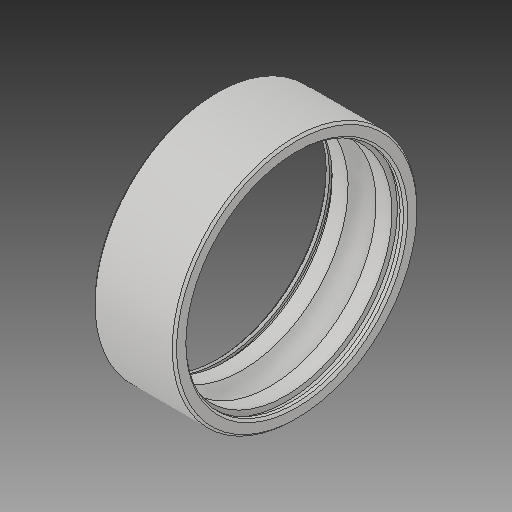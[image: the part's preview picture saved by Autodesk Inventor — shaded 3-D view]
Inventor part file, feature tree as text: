
AUTODESK INVENTOR PART (.ipt)
format: ipt  version: 2019 (Build 230136000, 136)  size: 173,568 bytes
history: mixed  units: mm
features: chamfer x1, imported_body x1
ambient origin geometry x8: Origin, YZ Plane, XZ Plane, XY Plane, X Axis, Y Axis, Z Axis, Center Point
bodies: Solid1 (imported_parasolid)
feature tree (2):
  chamfer  "Chamfer1"  [1 undecoded]
  imported_body  NMx_Import_Brep_tag  [imported B-rep: ~18 faces, bbox_mm=[3.0, 9.0, 0.0]]
note: 1 required parameter value undecoded (feature->parameter linkage not recoverable at this tier; creation-order binding heuristic only, values carry confidence <= 0.55)
